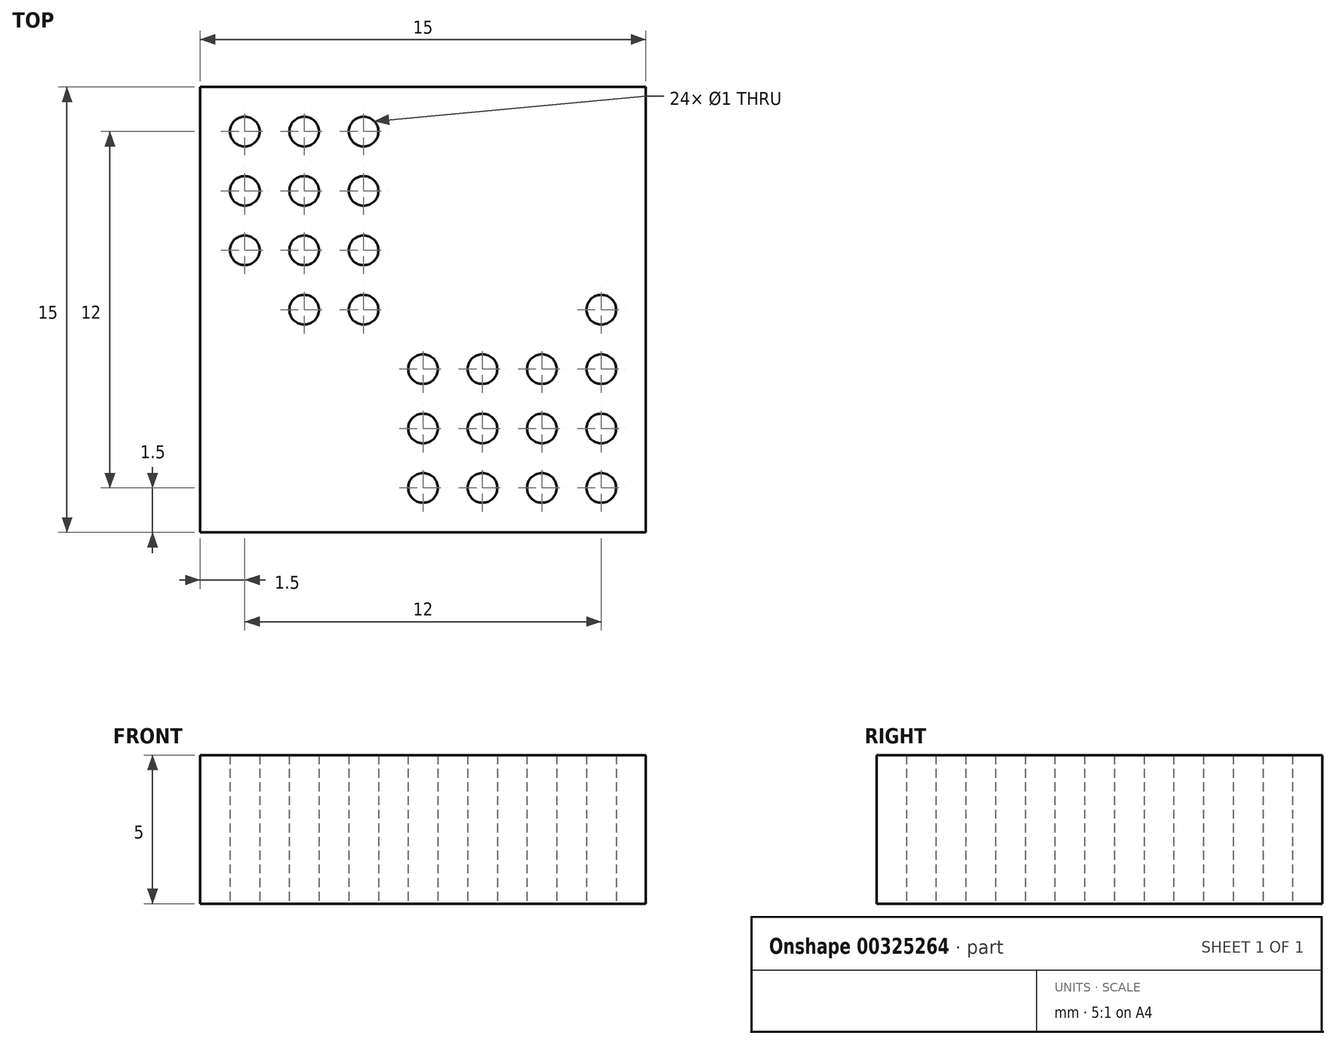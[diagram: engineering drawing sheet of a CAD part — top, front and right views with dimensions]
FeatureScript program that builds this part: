
annotation { "Feature Type Name" : "Feature", "Feature Type Description" : "" }
export const myFeature = defineFeature(function(context is Context, id is Id, definition is map)
    precondition{}
    {
        {
            var Q0;
            Q0=qCreatedBy(makeId("Top.planeOp"),FACE);
            var sketch = newSketch(context, id + "F0", { "sketchPlane" : qUnion([Q0])});
            skLineSegment(sketch, "E0.bottom", {"start": v(7.5, -7.5) * mm, "end": v(-7.5, -7.5) * mm});
            skLineSegment(sketch, "E0.top", {"start": v(7.5, 7.5) * mm, "end": v(-7.5, 7.5) * mm});
            skLineSegment(sketch, "E0.left", {"start": v(7.5, -7.5) * mm, "end": v(7.5, 7.5) * mm});
            skLineSegment(sketch, "E0.right", {"start": v(-7.5, -7.5) * mm, "end": v(-7.5, 7.5) * mm});
            skPoint(sketch, "E0.middle", {"position": v(0, 0) * mm});
            skCircle(sketch, "E1", {"center": v(0, 0) * mm, "radius": 0.5 * mm});
            skCircle(sketch, "E2.0.1.0", {"center": v(0, 2) * mm, "radius": 0.5 * mm});
            skCircle(sketch, "E2.0.2.0", {"center": v(0, 4) * mm, "radius": 0.5 * mm});
            skCircle(sketch, "E2.0.3.0", {"center": v(0, 6) * mm, "radius": 0.5 * mm});
            skCircle(sketch, "E2.1.0.0", {"center": v(2, 0) * mm, "radius": 0.5 * mm});
            skCircle(sketch, "E2.1.1.0", {"center": v(2, 2) * mm, "radius": 0.5 * mm});
            skCircle(sketch, "E2.1.2.0", {"center": v(2, 4) * mm, "radius": 0.5 * mm});
            skCircle(sketch, "E2.1.3.0", {"center": v(2, 6) * mm, "radius": 0.5 * mm});
            skCircle(sketch, "E2.2.0.0", {"center": v(4, 0) * mm, "radius": 0.5 * mm});
            skCircle(sketch, "E2.2.1.0", {"center": v(4, 2) * mm, "radius": 0.5 * mm});
            skCircle(sketch, "E2.2.2.0", {"center": v(4, 4) * mm, "radius": 0.5 * mm});
            skCircle(sketch, "E2.2.3.0", {"center": v(4, 6) * mm, "radius": 0.5 * mm});
            skCircle(sketch, "E2.3.1.0", {"center": v(6, 2) * mm, "radius": 0.5 * mm});
            skCircle(sketch, "E2.3.2.0", {"center": v(6, 4) * mm, "radius": 0.5 * mm});
            skCircle(sketch, "E2.3.3.0", {"center": v(6, 6) * mm, "radius": 0.5 * mm});
            skLineSegment(sketch, "E2.direction1", {"start": v(0, 0) * mm, "end": v(2, 0) * mm, "construction": true});
            skLineSegment(sketch, "E2.direction2", {"start": v(0, 0) * mm, "end": v(0, 2) * mm, "construction": true});
            skCircle(sketch, "E3.MirrorC", {"center": v(6, 0) * mm, "radius": 0.5 * mm});
            skCircle(sketch, "E4.MirrorC", {"center": v(6, -4) * mm, "radius": 0.5 * mm});
            skLineSegment(sketch, "E5.MirrorCS", {"start": v(0, 0) * mm, "end": v(0, -2) * mm, "construction": true});
            skCircle(sketch, "E6.MirrorC", {"center": v(2, -6) * mm, "radius": 0.5 * mm});
            skCircle(sketch, "E7.MirrorC", {"center": v(2, -4) * mm, "radius": 0.5 * mm});
            skCircle(sketch, "E8.MirrorC", {"center": v(2, -2) * mm, "radius": 0.5 * mm});
            skCircle(sketch, "E9.MirrorC", {"center": v(0, -6) * mm, "radius": 0.5 * mm});
            skCircle(sketch, "E10.MirrorC", {"center": v(0, -4) * mm, "radius": 0.5 * mm});
            skCircle(sketch, "E11.MirrorC", {"center": v(0, -2) * mm, "radius": 0.5 * mm});
            skCircle(sketch, "E12.MirrorC", {"center": v(4, -6) * mm, "radius": 0.5 * mm});
            skCircle(sketch, "E13.MirrorC", {"center": v(4, -4) * mm, "radius": 0.5 * mm});
            skCircle(sketch, "E14.MirrorC", {"center": v(6, -2) * mm, "radius": 0.5 * mm});
            skCircle(sketch, "E15.MirrorC", {"center": v(4, -2) * mm, "radius": 0.5 * mm});
            skCircle(sketch, "E16.MirrorC", {"center": v(6, -6) * mm, "radius": 0.5 * mm});
            skCircle(sketch, "E17.MirrorC", {"center": v(-2, 0) * mm, "radius": 0.5 * mm});
            skCircle(sketch, "E18.MirrorC", {"center": v(-6, -2) * mm, "radius": 0.5 * mm});
            skCircle(sketch, "E19.MirrorC", {"center": v(-6, 4) * mm, "radius": 0.5 * mm});
            skCircle(sketch, "E20.MirrorC", {"center": v(-6, 0) * mm, "radius": 0.5 * mm});
            skCircle(sketch, "E21.MirrorC", {"center": v(-4, -4) * mm, "radius": 0.5 * mm});
            skCircle(sketch, "E22.MirrorC", {"center": v(-6, 2) * mm, "radius": 0.5 * mm});
            skCircle(sketch, "E23.MirrorC", {"center": v(-2, -2) * mm, "radius": 0.5 * mm});
            skCircle(sketch, "E24.MirrorC", {"center": v(-4, 0) * mm, "radius": 0.5 * mm});
            skCircle(sketch, "E25.MirrorC", {"center": v(-2, 6) * mm, "radius": 0.5 * mm});
            skCircle(sketch, "E26.MirrorC", {"center": v(-2, -4) * mm, "radius": 0.5 * mm});
            skCircle(sketch, "E27.MirrorC", {"center": v(-4, -6) * mm, "radius": 0.5 * mm});
            skLineSegment(sketch, "E28.MirrorCS", {"start": v(0, 0) * mm, "end": v(-2, 0) * mm, "construction": true});
            skCircle(sketch, "E29.MirrorC", {"center": v(-4, 2) * mm, "radius": 0.5 * mm});
            skCircle(sketch, "E30.MirrorC", {"center": v(-6, -6) * mm, "radius": 0.5 * mm});
            skCircle(sketch, "E31.MirrorC", {"center": v(-4, 4) * mm, "radius": 0.5 * mm});
            skCircle(sketch, "E32.MirrorC", {"center": v(-4, 6) * mm, "radius": 0.5 * mm});
            skCircle(sketch, "E33.MirrorC", {"center": v(-6, 6) * mm, "radius": 0.5 * mm});
            skCircle(sketch, "E34.MirrorC", {"center": v(-6, -4) * mm, "radius": 0.5 * mm});
            skCircle(sketch, "E35.MirrorC", {"center": v(-2, -6) * mm, "radius": 0.5 * mm});
            skCircle(sketch, "E36.MirrorC", {"center": v(-4, -2) * mm, "radius": 0.5 * mm});
            skCircle(sketch, "E37.MirrorC", {"center": v(-2, 2) * mm, "radius": 0.5 * mm});
            skCircle(sketch, "E38.MirrorC", {"center": v(-2, 4) * mm, "radius": 0.5 * mm});
            skSolve(sketch);
        }
        {
            var Q0;
            Q0=makeQuery(id+"F0.imprint","IMPRINT",FACE,{"disambiguationData":[TD([[makeQuery(id+"F0.imprint","IMPRINT",EDGE,{"derivedFrom":sQuery(id+"F0.wireOp",EDGE,"E0.bottom")}),-1.0]])]});
            extrude(context, id + "F1", {"entities" : qUnion([Q0]), "depth" : 1 * mm});
        }
        {
            var Q0;
            Q0=makeQuery(id+"F0.imprint","IMPRINT",FACE,{"disambiguationData":[TD([[makeQuery(id+"F0.imprint","IMPRINT",EDGE,{"derivedFrom":sQuery(id+"F0.wireOp",EDGE,"E33.MirrorC")}),-1.0]])]});
            var Q1;
            Q1=makeQuery(id+"F0.imprint","IMPRINT",FACE,{"disambiguationData":[TD([[makeQuery(id+"F0.imprint","IMPRINT",EDGE,{"derivedFrom":sQuery(id+"F0.wireOp",EDGE,"E32.MirrorC")}),-1.0]])]});
            var Q2;
            Q2=makeQuery(id+"F0.imprint","IMPRINT",FACE,{"disambiguationData":[TD([[makeQuery(id+"F0.imprint","IMPRINT",EDGE,{"derivedFrom":sQuery(id+"F0.wireOp",EDGE,"E25.MirrorC")}),-1.0]])]});
            var Q3;
            Q3=makeQuery(id+"F0.imprint","IMPRINT",FACE,{"disambiguationData":[TD([[makeQuery(id+"F0.imprint","IMPRINT",EDGE,{"derivedFrom":sQuery(id+"F0.wireOp",EDGE,"E2.0.3.0")}),1.0]])]});
            var Q4;
            Q4=makeQuery(id+"F0.imprint","IMPRINT",FACE,{"disambiguationData":[TD([[makeQuery(id+"F0.imprint","IMPRINT",EDGE,{"derivedFrom":sQuery(id+"F0.wireOp",EDGE,"E2.1.3.0")}),1.0]])]});
            var Q5;
            Q5=makeQuery(id+"F0.imprint","IMPRINT",FACE,{"disambiguationData":[TD([[makeQuery(id+"F0.imprint","IMPRINT",EDGE,{"derivedFrom":sQuery(id+"F0.wireOp",EDGE,"E2.2.3.0")}),1.0]])]});
            var Q6;
            Q6=makeQuery(id+"F0.imprint","IMPRINT",FACE,{"disambiguationData":[TD([[makeQuery(id+"F0.imprint","IMPRINT",EDGE,{"derivedFrom":sQuery(id+"F0.wireOp",EDGE,"E2.3.3.0")}),1.0]])]});
            var Q7;
            Q7=makeQuery(id+"F0.imprint","IMPRINT",FACE,{"disambiguationData":[TD([[makeQuery(id+"F0.imprint","IMPRINT",EDGE,{"derivedFrom":sQuery(id+"F0.wireOp",EDGE,"E2.3.2.0")}),1.0]])]});
            var Q8;
            Q8=makeQuery(id+"F0.imprint","IMPRINT",FACE,{"disambiguationData":[TD([[makeQuery(id+"F0.imprint","IMPRINT",EDGE,{"derivedFrom":sQuery(id+"F0.wireOp",EDGE,"E2.2.2.0")}),1.0]])]});
            var Q9;
            Q9=makeQuery(id+"F0.imprint","IMPRINT",FACE,{"disambiguationData":[TD([[makeQuery(id+"F0.imprint","IMPRINT",EDGE,{"derivedFrom":sQuery(id+"F0.wireOp",EDGE,"E2.1.2.0")}),1.0]])]});
            var Q10;
            Q10=makeQuery(id+"F0.imprint","IMPRINT",FACE,{"disambiguationData":[TD([[makeQuery(id+"F0.imprint","IMPRINT",EDGE,{"derivedFrom":sQuery(id+"F0.wireOp",EDGE,"E2.0.2.0")}),1.0]])]});
            var Q11;
            Q11=makeQuery(id+"F0.imprint","IMPRINT",FACE,{"disambiguationData":[TD([[makeQuery(id+"F0.imprint","IMPRINT",EDGE,{"derivedFrom":sQuery(id+"F0.wireOp",EDGE,"E38.MirrorC")}),-1.0]])]});
            var Q12;
            Q12=makeQuery(id+"F0.imprint","IMPRINT",FACE,{"disambiguationData":[TD([[makeQuery(id+"F0.imprint","IMPRINT",EDGE,{"derivedFrom":sQuery(id+"F0.wireOp",EDGE,"E31.MirrorC")}),-1.0]])]});
            var Q13;
            Q13=makeQuery(id+"F0.imprint","IMPRINT",FACE,{"disambiguationData":[TD([[makeQuery(id+"F0.imprint","IMPRINT",EDGE,{"derivedFrom":sQuery(id+"F0.wireOp",EDGE,"E19.MirrorC")}),-1.0]])]});
            var Q14;
            Q14=makeQuery(id+"F0.imprint","IMPRINT",FACE,{"disambiguationData":[TD([[makeQuery(id+"F0.imprint","IMPRINT",EDGE,{"derivedFrom":sQuery(id+"F0.wireOp",EDGE,"E22.MirrorC")}),-1.0]])]});
            var Q15;
            Q15=makeQuery(id+"F0.imprint","IMPRINT",FACE,{"disambiguationData":[TD([[makeQuery(id+"F0.imprint","IMPRINT",EDGE,{"derivedFrom":sQuery(id+"F0.wireOp",EDGE,"E29.MirrorC")}),-1.0]])]});
            var Q16;
            Q16=makeQuery(id+"F0.imprint","IMPRINT",FACE,{"disambiguationData":[TD([[makeQuery(id+"F0.imprint","IMPRINT",EDGE,{"derivedFrom":sQuery(id+"F0.wireOp",EDGE,"E37.MirrorC")}),-1.0]])]});
            var Q17;
            Q17=makeQuery(id+"F0.imprint","IMPRINT",FACE,{"disambiguationData":[TD([[makeQuery(id+"F0.imprint","IMPRINT",EDGE,{"derivedFrom":sQuery(id+"F0.wireOp",EDGE,"E2.0.1.0")}),1.0]])]});
            var Q18;
            Q18=makeQuery(id+"F0.imprint","IMPRINT",FACE,{"disambiguationData":[TD([[makeQuery(id+"F0.imprint","IMPRINT",EDGE,{"derivedFrom":sQuery(id+"F0.wireOp",EDGE,"E2.1.1.0")}),1.0]])]});
            var Q19;
            Q19=makeQuery(id+"F0.imprint","IMPRINT",FACE,{"disambiguationData":[TD([[makeQuery(id+"F0.imprint","IMPRINT",EDGE,{"derivedFrom":sQuery(id+"F0.wireOp",EDGE,"E2.2.1.0")}),1.0]])]});
            var Q20;
            Q20=makeQuery(id+"F0.imprint","IMPRINT",FACE,{"disambiguationData":[TD([[makeQuery(id+"F0.imprint","IMPRINT",EDGE,{"derivedFrom":sQuery(id+"F0.wireOp",EDGE,"E2.3.1.0")}),1.0]])]});
            var Q21;
            Q21=makeQuery(id+"F0.imprint","IMPRINT",FACE,{"disambiguationData":[TD([[makeQuery(id+"F0.imprint","IMPRINT",EDGE,{"derivedFrom":sQuery(id+"F0.wireOp",EDGE,"E3.MirrorC")}),-1.0]])]});
            var Q22;
            Q22=makeQuery(id+"F0.imprint","IMPRINT",FACE,{"disambiguationData":[TD([[makeQuery(id+"F0.imprint","IMPRINT",EDGE,{"derivedFrom":sQuery(id+"F0.wireOp",EDGE,"E2.2.0.0")}),1.0]])]});
            var Q23;
            Q23=makeQuery(id+"F0.imprint","IMPRINT",FACE,{"disambiguationData":[TD([[makeQuery(id+"F0.imprint","IMPRINT",EDGE,{"derivedFrom":sQuery(id+"F0.wireOp",EDGE,"E2.1.0.0")}),1.0]])]});
            var Q24;
            Q24=makeQuery(id+"F0.imprint","IMPRINT",FACE,{"disambiguationData":[TD([[makeQuery(id+"F0.imprint","IMPRINT",EDGE,{"derivedFrom":sQuery(id+"F0.wireOp",EDGE,"E1")}),1.0]])]});
            var Q25;
            Q25=makeQuery(id+"F0.imprint","IMPRINT",FACE,{"disambiguationData":[TD([[makeQuery(id+"F0.imprint","IMPRINT",EDGE,{"derivedFrom":sQuery(id+"F0.wireOp",EDGE,"E17.MirrorC")}),-1.0]])]});
            var Q26;
            Q26=makeQuery(id+"F0.imprint","IMPRINT",FACE,{"disambiguationData":[TD([[makeQuery(id+"F0.imprint","IMPRINT",EDGE,{"derivedFrom":sQuery(id+"F0.wireOp",EDGE,"E24.MirrorC")}),-1.0]])]});
            var Q27;
            Q27=makeQuery(id+"F0.imprint","IMPRINT",FACE,{"disambiguationData":[TD([[makeQuery(id+"F0.imprint","IMPRINT",EDGE,{"derivedFrom":sQuery(id+"F0.wireOp",EDGE,"E20.MirrorC")}),1.0]])]});
            var Q28;
            Q28=makeQuery(id+"F0.imprint","IMPRINT",FACE,{"disambiguationData":[TD([[makeQuery(id+"F0.imprint","IMPRINT",EDGE,{"derivedFrom":sQuery(id+"F0.wireOp",EDGE,"E18.MirrorC")}),1.0]])]});
            var Q29;
            Q29=makeQuery(id+"F0.imprint","IMPRINT",FACE,{"disambiguationData":[TD([[makeQuery(id+"F0.imprint","IMPRINT",EDGE,{"derivedFrom":sQuery(id+"F0.wireOp",EDGE,"E36.MirrorC")}),1.0]])]});
            var Q30;
            Q30=makeQuery(id+"F0.imprint","IMPRINT",FACE,{"disambiguationData":[TD([[makeQuery(id+"F0.imprint","IMPRINT",EDGE,{"derivedFrom":sQuery(id+"F0.wireOp",EDGE,"E23.MirrorC")}),1.0]])]});
            var Q31;
            Q31=makeQuery(id+"F0.imprint","IMPRINT",FACE,{"disambiguationData":[TD([[makeQuery(id+"F0.imprint","IMPRINT",EDGE,{"derivedFrom":sQuery(id+"F0.wireOp",EDGE,"E11.MirrorC")}),-1.0]])]});
            var Q32;
            Q32=makeQuery(id+"F0.imprint","IMPRINT",FACE,{"disambiguationData":[TD([[makeQuery(id+"F0.imprint","IMPRINT",EDGE,{"derivedFrom":sQuery(id+"F0.wireOp",EDGE,"E8.MirrorC")}),-1.0]])]});
            var Q33;
            Q33=makeQuery(id+"F0.imprint","IMPRINT",FACE,{"disambiguationData":[TD([[makeQuery(id+"F0.imprint","IMPRINT",EDGE,{"derivedFrom":sQuery(id+"F0.wireOp",EDGE,"E15.MirrorC")}),-1.0]])]});
            var Q34;
            Q34=makeQuery(id+"F0.imprint","IMPRINT",FACE,{"disambiguationData":[TD([[makeQuery(id+"F0.imprint","IMPRINT",EDGE,{"derivedFrom":sQuery(id+"F0.wireOp",EDGE,"E14.MirrorC")}),-1.0]])]});
            var Q35;
            Q35=makeQuery(id+"F0.imprint","IMPRINT",FACE,{"disambiguationData":[TD([[makeQuery(id+"F0.imprint","IMPRINT",EDGE,{"derivedFrom":sQuery(id+"F0.wireOp",EDGE,"E4.MirrorC")}),-1.0]])]});
            var Q36;
            Q36=makeQuery(id+"F0.imprint","IMPRINT",FACE,{"disambiguationData":[TD([[makeQuery(id+"F0.imprint","IMPRINT",EDGE,{"derivedFrom":sQuery(id+"F0.wireOp",EDGE,"E13.MirrorC")}),-1.0]])]});
            var Q37;
            Q37=makeQuery(id+"F0.imprint","IMPRINT",FACE,{"disambiguationData":[TD([[makeQuery(id+"F0.imprint","IMPRINT",EDGE,{"derivedFrom":sQuery(id+"F0.wireOp",EDGE,"E7.MirrorC")}),-1.0]])]});
            var Q38;
            Q38=makeQuery(id+"F0.imprint","IMPRINT",FACE,{"disambiguationData":[TD([[makeQuery(id+"F0.imprint","IMPRINT",EDGE,{"derivedFrom":sQuery(id+"F0.wireOp",EDGE,"E10.MirrorC")}),-1.0]])]});
            var Q39;
            Q39=makeQuery(id+"F0.imprint","IMPRINT",FACE,{"disambiguationData":[TD([[makeQuery(id+"F0.imprint","IMPRINT",EDGE,{"derivedFrom":sQuery(id+"F0.wireOp",EDGE,"E26.MirrorC")}),1.0]])]});
            var Q40;
            Q40=makeQuery(id+"F0.imprint","IMPRINT",FACE,{"disambiguationData":[TD([[makeQuery(id+"F0.imprint","IMPRINT",EDGE,{"derivedFrom":sQuery(id+"F0.wireOp",EDGE,"E21.MirrorC")}),1.0]])]});
            var Q41;
            Q41=makeQuery(id+"F0.imprint","IMPRINT",FACE,{"disambiguationData":[TD([[makeQuery(id+"F0.imprint","IMPRINT",EDGE,{"derivedFrom":sQuery(id+"F0.wireOp",EDGE,"E34.MirrorC")}),1.0]])]});
            var Q42;
            Q42=makeQuery(id+"F0.imprint","IMPRINT",FACE,{"disambiguationData":[TD([[makeQuery(id+"F0.imprint","IMPRINT",EDGE,{"derivedFrom":sQuery(id+"F0.wireOp",EDGE,"E30.MirrorC")}),1.0]])]});
            var Q43;
            Q43=makeQuery(id+"F0.imprint","IMPRINT",FACE,{"disambiguationData":[TD([[makeQuery(id+"F0.imprint","IMPRINT",EDGE,{"derivedFrom":sQuery(id+"F0.wireOp",EDGE,"E27.MirrorC")}),1.0]])]});
            var Q44;
            Q44=makeQuery(id+"F0.imprint","IMPRINT",FACE,{"disambiguationData":[TD([[makeQuery(id+"F0.imprint","IMPRINT",EDGE,{"derivedFrom":sQuery(id+"F0.wireOp",EDGE,"E35.MirrorC")}),1.0]])]});
            var Q45;
            Q45=makeQuery(id+"F0.imprint","IMPRINT",FACE,{"disambiguationData":[TD([[makeQuery(id+"F0.imprint","IMPRINT",EDGE,{"derivedFrom":sQuery(id+"F0.wireOp",EDGE,"E9.MirrorC")}),-1.0]])]});
            var Q46;
            Q46=makeQuery(id+"F0.imprint","IMPRINT",FACE,{"disambiguationData":[TD([[makeQuery(id+"F0.imprint","IMPRINT",EDGE,{"derivedFrom":sQuery(id+"F0.wireOp",EDGE,"E6.MirrorC")}),-1.0]])]});
            var Q47;
            Q47=makeQuery(id+"F0.imprint","IMPRINT",FACE,{"disambiguationData":[TD([[makeQuery(id+"F0.imprint","IMPRINT",EDGE,{"derivedFrom":sQuery(id+"F0.wireOp",EDGE,"E12.MirrorC")}),-1.0]])]});
            var Q48;
            Q48=makeQuery(id+"F0.imprint","IMPRINT",FACE,{"disambiguationData":[TD([[makeQuery(id+"F0.imprint","IMPRINT",EDGE,{"derivedFrom":sQuery(id+"F0.wireOp",EDGE,"E16.MirrorC")}),-1.0]])]});
            extrude(context, id + "F2", {"entities" : qUnion([Q0, Q1, Q2, Q3, Q4, Q5, Q6, Q7, Q8, Q9, Q10, Q11, Q12, Q13, Q14, Q15, Q16, Q17, Q18, Q19, Q20, Q21, Q22, Q23, Q24, Q25, Q26, Q27, Q28, Q29, Q30, Q31, Q32, Q33, Q34, Q35, Q36, Q37, Q38, Q39, Q40, Q41, Q42, Q43, Q44, Q45, Q46, Q47, Q48]), "operationType" : NewBodyOperationType.ADD, "depth" : 5 * mm});
        }
    });
